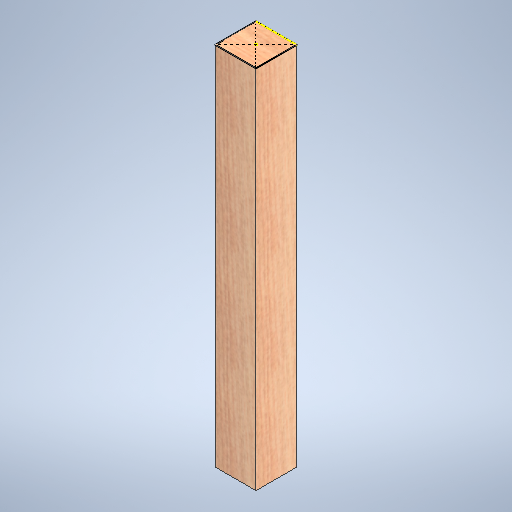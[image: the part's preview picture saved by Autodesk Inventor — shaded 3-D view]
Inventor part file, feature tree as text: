
AUTODESK INVENTOR PART (.ipt)
format: ipt  version: 2025 (Build 290162000, 162)  size: 347,648 bytes
history: native  units: in
note: dims shown in document units (in); Inventor stores cm internally (conversion verified against a paired STEP export)
features: sketch x2, extrude x1
ambient origin geometry x8: Origin, YZ Plane, XZ Plane, XY Plane, X Axis, Y Axis, Z Axis, Center Point
bodies: Solid1 (feature_tree)
feature tree (3):
  extrude  "Extrusion1"  Depth=4.0in
  sketch  "Sketch2"  dims[d2=36.0in d3=0.0in d4=0.5in d5=0.0344in d6=0.5in d7=0.0344in]
  sketch  "Sketch1"  dims[d0=4.0in d1=4.0in]
